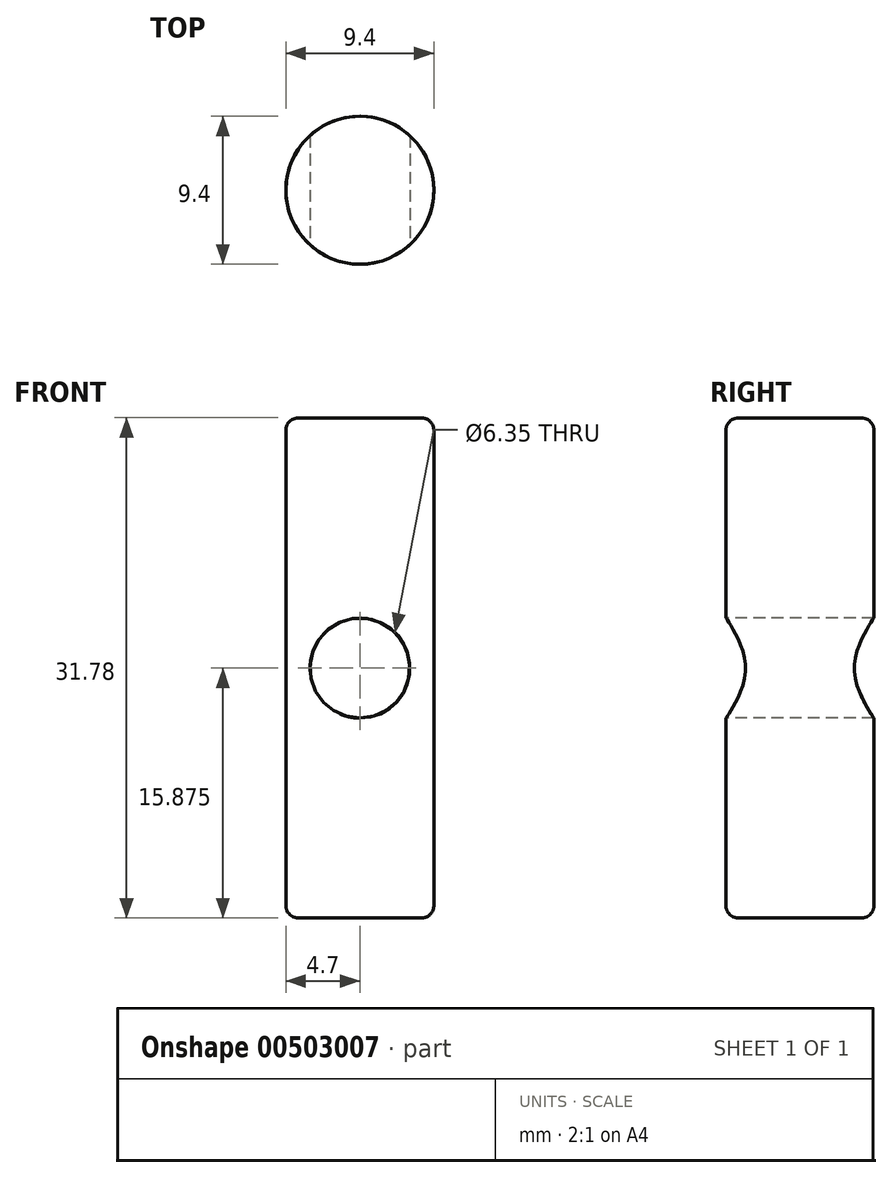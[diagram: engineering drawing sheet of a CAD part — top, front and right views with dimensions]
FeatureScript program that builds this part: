
annotation { "Feature Type Name" : "Feature", "Feature Type Description" : "" }
export const myFeature = defineFeature(function(context is Context, id is Id, definition is map)
    precondition{}
    {
        {
            var Q0;
            Q0=qCreatedBy(makeId("Top.planeOp"),FACE);
            var sketch = newSketch(context, id + "F0", { "sketchPlane" : qUnion([Q0])});
            skCircle(sketch, "E0", {"center": v(0, 0) * mm, "radius": 4.7 * mm});
            skSolve(sketch);
        }
        {
            var Q0;
            Q0 = qSketchRegion(id + "F0", true);
            extrude(context, id + "F1", {"entities" : qUnion([Q0]), "depth" : 31.78 * mm});
        }
        {
            var Q0;
            Q0=qCreatedBy(makeId("Front.planeOp"),FACE);
            var sketch = newSketch(context, id + "F2", { "sketchPlane" : qUnion([Q0])});
            skCircle(sketch, "E1", {"center": v(0, 15.88) * mm, "radius": 3.18 * mm});
            skSolve(sketch);
        }
        {
            var Q0;
            Q0 = qSketchRegion(id + "F2", true);
            extrude(context, id + "F3", {"entities" : qUnion([Q0]), "operationType" : NewBodyOperationType.REMOVE, "oppositeDirection" : true, "depth" : 15 * mm, "hasSecondDirection" : true, "secondDirectionOppositeDirection" : false, "secondDirectionDepth" : 25.4 * mm});
        }
        {
            var Q0;
            Q0=makeQuery(id+"F1.opExtrude","CAP_EDGE",EDGE,{"disambiguationData":[OSD([sQuery(id+"F0.wireOp",EDGE,"E0")])],"isStart":false});
            var Q1;
            Q1=makeQuery(id+"F1.opExtrude","CAP_EDGE",EDGE,{"disambiguationData":[OSD([sQuery(id+"F0.wireOp",EDGE,"E0")])],"isStart":true});
            fillet(context, id + "F4", {"entities" : qUnion([Q0, Q1]), "radius" : 0.8 * mm, "tangentPropagation" : true, "allowEdgeOverflow" : false});
        }
    });
